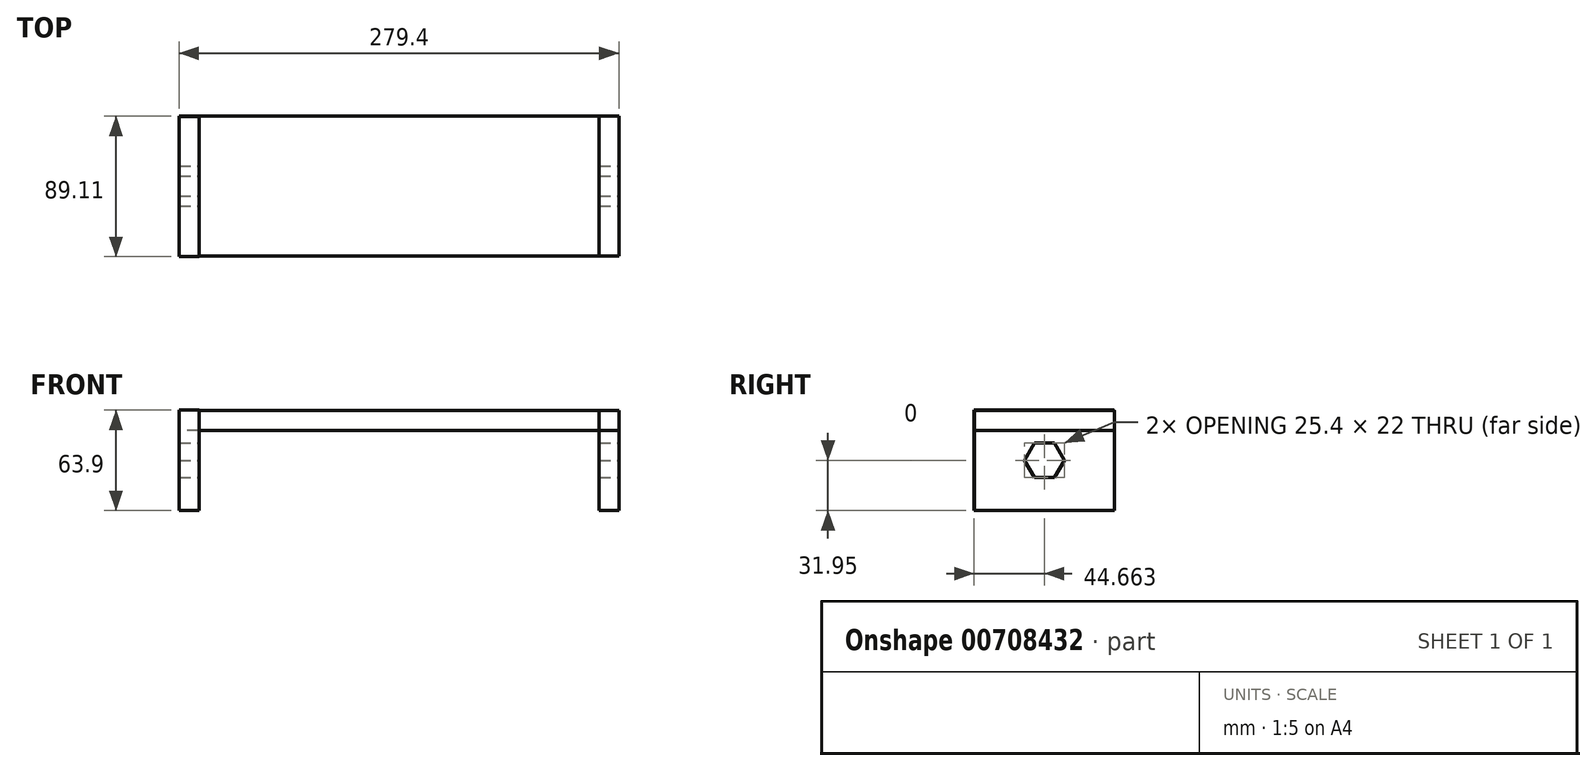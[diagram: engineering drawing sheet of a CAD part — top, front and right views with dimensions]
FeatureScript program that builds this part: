
annotation { "Feature Type Name" : "Feature", "Feature Type Description" : "" }
export const myFeature = defineFeature(function(context is Context, id is Id, definition is map)
    precondition{}
    {
        {
            var Q0;
            Q0=qCreatedBy(makeId("Right.planeOp"),FACE);
            var sketch = newSketch(context, id + "F0", { "sketchPlane" : qUnion([Q0])});
            skLineSegment(sketch, "E0.bottom", {"start": v(-67.79, 47.99) * mm, "end": v(21.11, 47.99) * mm});
            skLineSegment(sketch, "E0.top", {"start": v(-67.79, -15.51) * mm, "end": v(21.11, -15.51) * mm});
            skLineSegment(sketch, "E0.left", {"start": v(-67.79, 47.99) * mm, "end": v(-67.79, -15.51) * mm});
            skLineSegment(sketch, "E0.right", {"start": v(21.11, 47.99) * mm, "end": v(21.11, -15.51) * mm});
            skPoint(sketch, "E0.middle", {"position": v(-23.34, 16.24) * mm});
            skSolve(sketch);
        }
        {
            var Q0;
            Q0=makeQuery(id+"F0.imprint","IMPRINT",FACE,{"disambiguationData":[TD([[makeQuery(id+"F0.imprint","IMPRINT",EDGE,{"derivedFrom":sQuery(id+"F0.wireOp",EDGE,"E0.bottom")}),-1.0]])]});
            extrude(context, id + "F1", {"entities" : qUnion([Q0]), "depth" : 12.7 * mm, "offsetDistance" : 25.4 * mm});
        }
        {
            var Q0;
            Q0=qCreatedBy(makeId("Right.planeOp"),FACE);
            cPlane(context, id + "F2", {"entities" : qUnion([Q0]), "cplaneType" : CPlaneType.OFFSET, "offset" : 254 * mm, "oppositeDirection" : true, "width" : 152.4 * mm, "height" : 152.4 * mm});
        }
        {
            var Q0;
            Q0=qCreatedBy(id+"F2.planeOp",FACE);
            var sketch = newSketch(context, id + "F3", { "sketchPlane" : qUnion([Q0])});
            skLineSegment(sketch, "E1.bottom", {"start": v(21, 48.2) * mm, "end": v(-68, 48.2) * mm});
            skLineSegment(sketch, "E1.top", {"start": v(21, -15.71) * mm, "end": v(-68, -15.71) * mm});
            skLineSegment(sketch, "E1.left", {"start": v(21, 48.2) * mm, "end": v(21, -15.71) * mm});
            skLineSegment(sketch, "E1.right", {"start": v(-68, 48.2) * mm, "end": v(-68, -15.71) * mm});
            skSolve(sketch);
        }
        {
            var Q0;
            Q0=makeQuery(id+"F3.imprint","IMPRINT",FACE,{"disambiguationData":[TD([[makeQuery(id+"F3.imprint","IMPRINT",EDGE,{"derivedFrom":sQuery(id+"F3.wireOp",EDGE,"E1.bottom")}),1.0]])]});
            extrude(context, id + "F4", {"entities" : qUnion([Q0]), "oppositeDirection" : true, "depth" : 12.7 * mm, "offsetDistance" : 25.4 * mm});
        }
        {
            var Q0;
            Q0=makeQuery(id+"F1.opExtrude","CAP_FACE",FACE,{"disambiguationData":[OSD([sQuery(id+"F0.wireOp",EDGE,"E0.bottom"),sQuery(id+"F0.wireOp",EDGE,"E0.top"),sQuery(id+"F0.wireOp",EDGE,"E0.left"),sQuery(id+"F0.wireOp",EDGE,"E0.right")])],"isStart":false});
            var sketch = newSketch(context, id + "F5", { "sketchPlane" : qUnion([Q0])});
            skCircle(sketch, "E2.cCircle", {"center": v(-23.34, 16.24) * mm, "radius": 12.7 * mm, "construction": true});
            skPoint(sketch, "E2.cCircle.centerSnap0", {"position": v(21.11, 16.24) * mm});
            skPoint(sketch, "E2.cCircle.centerSnap1", {"position": v(-23.34, 47.99) * mm});
            skPoint(sketch, "E2.cCircle.perimeterSnap0", {"position": v(21.11, 16.24) * mm});
            skLineSegment(sketch, "E2.0", {"start": v(-10.64, 16.24) * mm, "end": v(-16.99, 5.24) * mm});
            skPoint(sketch, "E2.0.startSnap0", {"position": v(21.11, 16.24) * mm});
            skLineSegment(sketch, "E2.1", {"start": v(-16.99, 5.24) * mm, "end": v(-29.69, 5.24) * mm});
            skLineSegment(sketch, "E2.2", {"start": v(-29.69, 5.24) * mm, "end": v(-36.04, 16.24) * mm});
            skLineSegment(sketch, "E2.3", {"start": v(-36.04, 16.24) * mm, "end": v(-29.69, 27.24) * mm});
            skLineSegment(sketch, "E2.4", {"start": v(-29.69, 27.24) * mm, "end": v(-16.99, 27.24) * mm});
            skLineSegment(sketch, "E2.5", {"start": v(-16.99, 27.24) * mm, "end": v(-10.64, 16.24) * mm});
            skSolve(sketch);
        }
        {
            var Q0;
            Q0=makeQuery(id+"F1.opExtrude","SWEPT_FACE",FACE,{"disambiguationData":[OSD([sQuery(id+"F0.wireOp",EDGE,"E0.bottom")])]});
            var sketch = newSketch(context, id + "F6", { "sketchPlane" : qUnion([Q0])});
            skLineSegment(sketch, "E3.bottom", {"start": v(12.7, 21.11) * mm, "end": v(-266.7, 21.11) * mm});
            skLineSegment(sketch, "E3.top", {"start": v(12.7, -67.79) * mm, "end": v(-266.7, -67.79) * mm});
            skLineSegment(sketch, "E3.left", {"start": v(12.7, 21.11) * mm, "end": v(12.7, -67.79) * mm});
            skLineSegment(sketch, "E3.right", {"start": v(-266.7, 21.11) * mm, "end": v(-266.7, -67.79) * mm});
            skSolve(sketch);
        }
        {
            var Q0;
            {var subQ2=sQuery(id+"F6.wireOp",EDGE,"E3.right");Q0=makeQuery(id+"F6.imprint","IMPRINT",FACE,{"disambiguationData":[TD([[makeQuery(id+"F6.imprint","IMPRINT",EDGE,{"derivedFrom":subQ2}),1.0]])]});}
            var Q1;
            {var subQ2=sQuery(id+"F6.wireOp",EDGE,"E3.left");Q1=makeQuery(id+"F6.imprint","IMPRINT",FACE,{"disambiguationData":[TD([[makeQuery(id+"F6.imprint","IMPRINT",EDGE,{"derivedFrom":subQ2}),1.0]])]});}
            extrude(context, id + "F7", {"entities" : qUnion([Q0, Q1]), "oppositeDirection" : true, "depth" : 12.7 * mm, "offsetDistance" : 25.4 * mm});
        }
        {
            var Q0;
            Q0 = qSketchRegion(id + "F5", true);
            extrude(context, id + "F8", {"entities" : qUnion([Q0]), "operationType" : NewBodyOperationType.REMOVE, "oppositeDirection" : true, "depth" : 304.8 * mm, "offsetDistance" : 25.4 * mm});
        }
    });
